# Revit family: Блоки трансформаторные_АРИЯ
name_source: partatom
category: Системы пожарной сигнализации
revit_build: Autodesk Revit MEP 2016 (Build: 20151007_0715(x64)
units: mm (PartAtom-declared; Revit-internal decimal feet)

## family parameters
Общий = Нет
Основа = Грань
При загрузке вырезать с полостями = Нет
Размер круглого соединителя = Использовать диаметр
Сохранять ориентацию аннотаций = Нет
Тип детали = Нормальный
Точка расчета площади = Нет

## types (4) — shared parameters
A = 465 мм
ADSK_URL документации изделия = https://omelta.com
ADSK_URL страницы изделия = https://omelta.com
ADSK_Единица измерения = шт.
ADSK_Завод-изготовитель = г. Омск, ООО «Электротехника и Автоматика»
ADSK_Код изделия = 437245
ADSK_Напряжение = 220 В
ADSK_Размер_Высота = 45 мм
ADSK_Размер_Глубина = 275 мм
ADSK_Размер_Длина = 430 мм
ADSK_Размер_Ширина = 482 мм
IP = 20
Гарантийный срок службы = 3 года
Диапазон рабочих температур = –10...+55 °С
Материал_Корпус = ЭиА_Черный
Материал_Надпись = ЭиА_Белый
zero-valued in all types: Отметка по умолчанию

## per-type parameters (varying)
| type | ADSK_Масса | ADSK_Наименование | ADSK_Номинальная мощность | ADSK_Обозначение | ADSK_Ток | Выходная мощность | Количество зон |
| АРИЯ-ТС-БРО-РМ-2-120 | 4 | Блок речевого оповещения | 400 В·А | Блок речевого оповещения трансформаторный двухзональный с резервным источником питания и возможностью трансляции музыки | 2 мА | 240 Вт | 2 |
| АРИЯ-ТС-БР-РМ-2-120 | 3.75 | Блок расширения | 400 В·А | Блок расширения трансформаторный двухзональный с резервным источником питания и возможностью трансляции музыки | 2 мА | 240 Вт | 2 |
| АРИЯ-ТС-БРО-РМ-120 | 3.75 | Блок речевого оповещения | 200 В·А | Блок речевого оповещения трансформаторный однозональный с резервным источником питания и возможностью трансляции музыки | 1 мА | 120 Вт | 1 |
| АРИЯ-ТС-БР-РМ-120 | 3.6 | Блок расширения | 200 В·А | Блок расширения трансформаторный однозональный с резервным источником питания и возможностью трансляции музыки | 1 мА | 120 Вт | 1 |

note: column(s) folded — value = type name in every type: ADSK_Марка, Надпись

## geometry (parser evidence)
native form markers: Blend x2
no freeform markers — native parametric forms only
